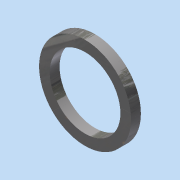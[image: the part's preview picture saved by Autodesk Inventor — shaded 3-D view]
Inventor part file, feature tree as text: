
AUTODESK INVENTOR PART (.ipt)
format: ipt  version: 2015 (Build 190159000, 159)  size: 83,456 bytes
history: native  units: in
note: dims shown in document units (in); Inventor stores cm internally (conversion verified against a paired STEP export)
features: extrude x1, sketch x1
ambient origin geometry x8: Origin, YZ Plane, XZ Plane, XY Plane, X Axis, Y Axis, Z Axis, Center Point
bodies: Solid1 (feature_tree)
feature tree (2):
  extrude  "Extrusion1"  Depth=0.2756in
  sketch  "Sketch1"  dims[d0=1.9685in d1=2.5591in d2=0.2756in d3=0.0in]
